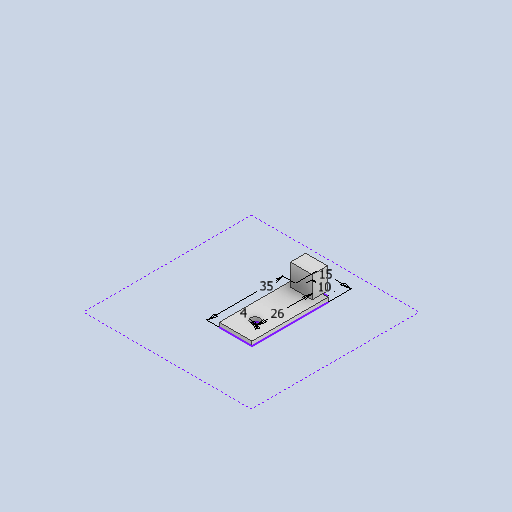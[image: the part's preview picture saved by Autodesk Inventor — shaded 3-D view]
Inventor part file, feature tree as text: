
AUTODESK INVENTOR PART (.ipt)
format: ipt  version: 2025.1 (Build 291241000, 241)  size: 276,992 bytes
history: native  units: mm
features: extrude x2, sketch x1, other x1
ambient origin geometry x8: Origin, YZ Plane, XZ Plane, XY Plane, X Axis, Y Axis, Z Axis, Center Point
bodies: Solid1 (feature_tree)
feature tree (4):
  sketch  "Sketch1"  dims[d6=35.0mm d9=15.0mm d11=4.0mm d21=26.0mm d26=10.0mm d28=2.0mm d29=0.0mm d30=10.0mm d31=0.0mm]
  extrude  "Extrusion1"  Depth=15.0mm
  extrude  "Extrusion2"  Depth=10.0mm
  other  "Image1"
